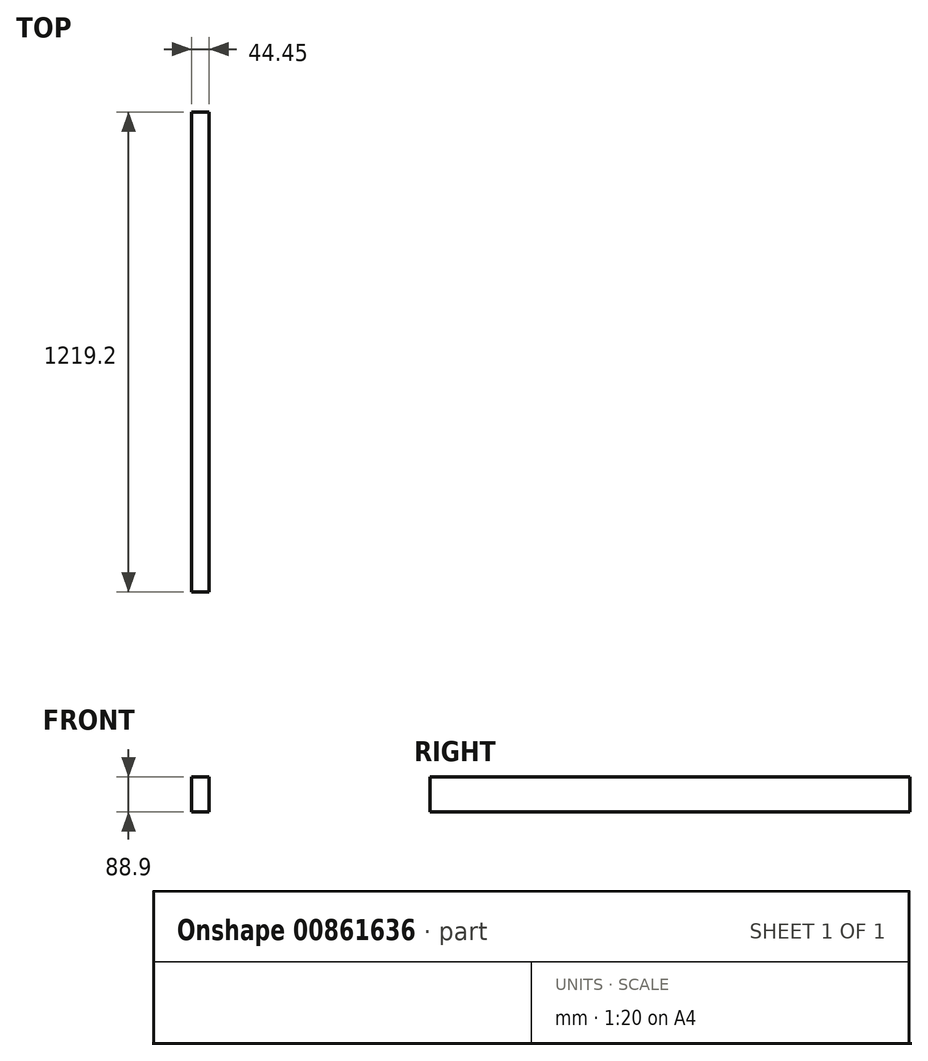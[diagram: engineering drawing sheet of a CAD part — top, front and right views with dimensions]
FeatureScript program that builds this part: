
annotation { "Feature Type Name" : "Feature", "Feature Type Description" : "" }
export const myFeature = defineFeature(function(context is Context, id is Id, definition is map)
    precondition{}
    {
        {
            var Q0;
            Q0=qCreatedBy(makeId("Front.planeOp"),FACE);
            var sketch = newSketch(context, id + "F0", { "sketchPlane" : qUnion([Q0])});
            skLineSegment(sketch, "E0.bottom", {"start": v(0, 0) * mm, "end": v(44.45, 0) * mm});
            skLineSegment(sketch, "E0.top", {"start": v(0, 88.9) * mm, "end": v(44.45, 88.9) * mm});
            skLineSegment(sketch, "E0.left", {"start": v(0, 0) * mm, "end": v(0, 88.9) * mm});
            skLineSegment(sketch, "E0.right", {"start": v(44.45, 0) * mm, "end": v(44.45, 88.9) * mm});
            skSolve(sketch);
        }
        {
            var Q0;
            Q0=makeQuery(id+"F0.imprint","IMPRINT",FACE,{"disambiguationData":[TD([[makeQuery(id+"F0.imprint","IMPRINT",EDGE,{"derivedFrom":sQuery(id+"F0.wireOp",EDGE,"E0.bottom")}),1.0]])]});
            extrude(context, id + "F1", {"entities" : qUnion([Q0]), "depth" : 1219.2 * mm, "offsetDistance" : 25.4 * mm});
        }
    });
